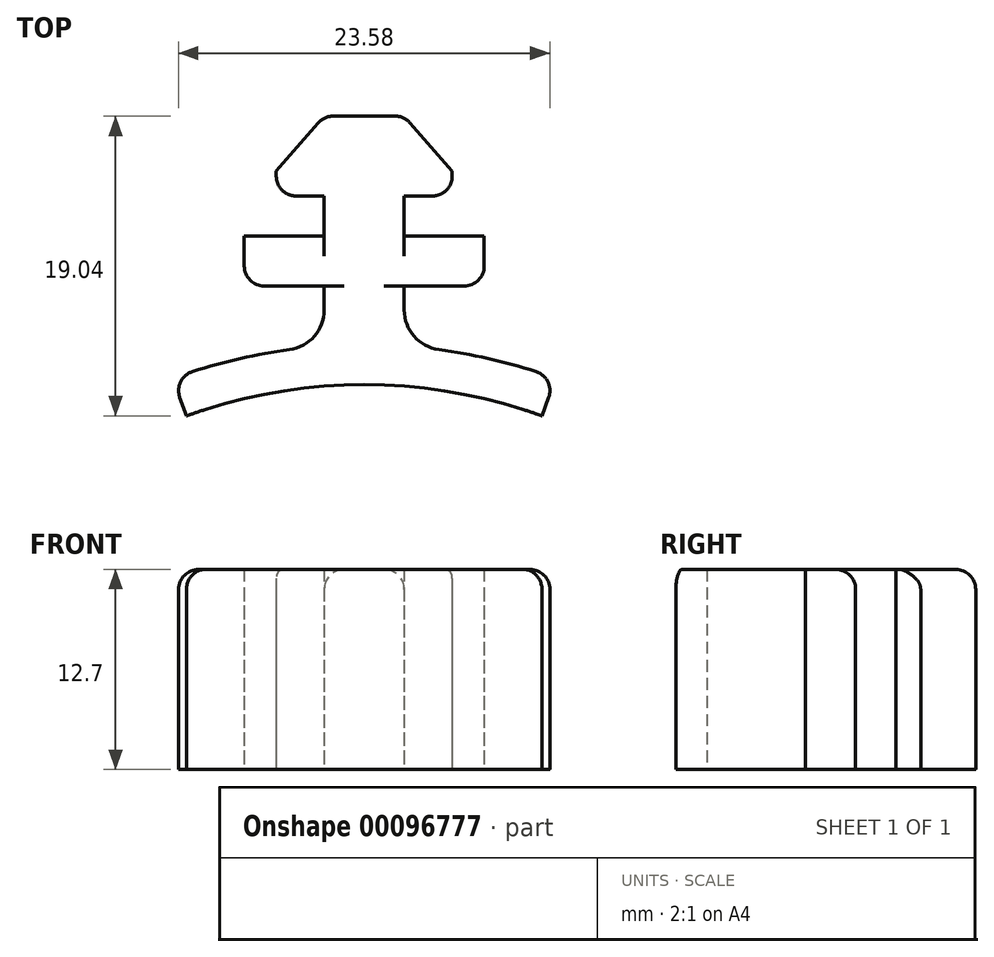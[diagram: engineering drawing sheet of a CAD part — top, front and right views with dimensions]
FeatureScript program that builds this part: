
annotation { "Feature Type Name" : "Feature", "Feature Type Description" : "" }
export const myFeature = defineFeature(function(context is Context, id is Id, definition is map)
    precondition{}
    {
        {
            var Q0;
            Q0=qCreatedBy(makeId("Top.planeOp"),FACE);
            var sketch = newSketch(context, id + "F0", { "sketchPlane" : qUnion([Q0])});
            skArc(sketch, "E0", {"start": v(11.29, 31) * mm, "mid": v(0, 33) * mm, "end": v(-11.29, 31) * mm});
            skArc(sketch, "E1.0", {"start": v(10.9, 33.82) * mm, "mid": v(7.86, 34.66) * mm, "end": v(4.74, 35.22) * mm});
            skLineSegment(sketch, "E2", {"start": v(0, 0) * mm, "end": v(0, 42.98) * mm, "construction": true});
            skLineSegment(sketch, "E3", {"start": v(11.29, 31) * mm, "end": v(11.71, 32.18) * mm});
            skLineSegment(sketch, "E4.MirrorCS", {"start": v(-11.29, 31) * mm, "end": v(-11.71, 32.18) * mm});
            skLineSegment(sketch, "E5", {"start": v(2.54, 37.74) * mm, "end": v(2.54, 39.26) * mm});
            skLineSegment(sketch, "E6.MirrorCS", {"start": v(-2.54, 37.74) * mm, "end": v(-2.54, 39.26) * mm});
            skLineSegment(sketch, "E7", {"start": v(2.54, 39.26) * mm, "end": v(6.35, 39.26) * mm});
            skLineSegment(sketch, "E8", {"start": v(7.62, 40.53) * mm, "end": v(7.62, 42.43) * mm});
            skLineSegment(sketch, "E9", {"start": v(7.62, 42.43) * mm, "end": v(2.54, 42.43) * mm});
            skLineSegment(sketch, "E10", {"start": v(2.54, 42.43) * mm, "end": v(2.54, 44.97) * mm});
            skLineSegment(sketch, "E11", {"start": v(2.54, 44.97) * mm, "end": v(4.32, 44.97) * mm});
            skLineSegment(sketch, "E12", {"start": v(5.59, 46.24) * mm, "end": v(5.59, 46.56) * mm});
            skLineSegment(sketch, "E13", {"start": v(5.59, 46.56) * mm, "end": v(2.92, 49.62) * mm});
            skLineSegment(sketch, "E14", {"start": v(1.96, 50.05) * mm, "end": v(0, 50.05) * mm});
            skLineSegment(sketch, "E15.MirrorCS", {"start": v(-5.59, 46.24) * mm, "end": v(-5.59, 46.56) * mm});
            skLineSegment(sketch, "E16.MirrorCS", {"start": v(-5.59, 46.56) * mm, "end": v(-2.92, 49.62) * mm});
            skLineSegment(sketch, "E17.MirrorCS", {"start": v(-2.54, 44.97) * mm, "end": v(-4.32, 44.97) * mm});
            skLineSegment(sketch, "E18.MirrorCS", {"start": v(-7.62, 42.43) * mm, "end": v(-2.54, 42.43) * mm});
            skLineSegment(sketch, "E19.MirrorCS", {"start": v(-2.54, 42.43) * mm, "end": v(-2.54, 44.97) * mm});
            skLineSegment(sketch, "E20.MirrorCS", {"start": v(-7.62, 40.53) * mm, "end": v(-7.62, 42.43) * mm});
            skLineSegment(sketch, "E21.MirrorCS", {"start": v(-2.54, 39.26) * mm, "end": v(-6.35, 39.26) * mm});
            skLineSegment(sketch, "E22.MirrorCS", {"start": v(-1.96, 50.05) * mm, "end": v(0, 50.05) * mm});
            skLineSegment(sketch, "E23.MirrorCS", {"start": v(-2.54, 50.05) * mm, "end": v(0, 50.05) * mm});
            skPoint(sketch, "E24.orphan", {"position": v(-15.23, 41.84) * mm});
            skPoint(sketch, "E25.orphan", {"position": v(15.23, 41.84) * mm});
            skArc(sketch, "E26.trimOffspring", {"start": v(-4.74, 35.22) * mm, "mid": v(-7.86, 34.66) * mm, "end": v(-10.9, 33.82) * mm});
            skPoint(sketch, "E27.visualSharp", {"position": v(-2.54, 35.45) * mm});
            skArc(sketch, "E27.filletArc", {"start": v(-4.74, 35.22) * mm, "mid": v(-3.17, 36.07) * mm, "end": v(-2.54, 37.74) * mm});
            skPoint(sketch, "E28.visualSharp", {"position": v(2.54, 35.45) * mm});
            skArc(sketch, "E28.filletArc", {"start": v(2.54, 37.74) * mm, "mid": v(3.17, 36.07) * mm, "end": v(4.74, 35.22) * mm});
            skPoint(sketch, "E29.visualSharp", {"position": v(-7.62, 39.26) * mm});
            skArc(sketch, "E29.filletArc", {"start": v(-7.62, 40.53) * mm, "mid": v(-7.25, 39.63) * mm, "end": v(-6.35, 39.26) * mm});
            skPoint(sketch, "E30.visualSharp", {"position": v(7.62, 39.26) * mm});
            skArc(sketch, "E30.filletArc", {"start": v(6.35, 39.26) * mm, "mid": v(7.25, 39.63) * mm, "end": v(7.62, 40.53) * mm});
            skPoint(sketch, "E31.visualSharp", {"position": v(12.16, 33.4) * mm});
            skArc(sketch, "E31.filletArc", {"start": v(11.71, 32.18) * mm, "mid": v(11.66, 33.17) * mm, "end": v(10.9, 33.82) * mm});
            skPoint(sketch, "E32.visualSharp", {"position": v(-12.16, 33.4) * mm});
            skArc(sketch, "E32.filletArc", {"start": v(-10.9, 33.82) * mm, "mid": v(-11.66, 33.17) * mm, "end": v(-11.71, 32.18) * mm});
            skPoint(sketch, "E33.visualSharp", {"position": v(-2.54, 50.05) * mm});
            skArc(sketch, "E33.filletArc", {"start": v(-1.96, 50.05) * mm, "mid": v(-2.49, 49.94) * mm, "end": v(-2.92, 49.62) * mm});
            skPoint(sketch, "E34.visualSharp", {"position": v(2.54, 50.05) * mm});
            skArc(sketch, "E34.filletArc", {"start": v(2.92, 49.62) * mm, "mid": v(2.49, 49.94) * mm, "end": v(1.96, 50.05) * mm});
            skPoint(sketch, "E35.visualSharp", {"position": v(-5.59, 44.97) * mm});
            skArc(sketch, "E35.filletArc", {"start": v(-5.59, 46.24) * mm, "mid": v(-5.22, 45.35) * mm, "end": v(-4.32, 44.97) * mm});
            skPoint(sketch, "E36.visualSharp", {"position": v(5.59, 44.97) * mm});
            skArc(sketch, "E36.filletArc", {"start": v(4.32, 44.97) * mm, "mid": v(5.22, 45.35) * mm, "end": v(5.59, 46.24) * mm});
            skSolve(sketch);
        }
        {
            var Q0;
            Q0=makeQuery(id+"F0.imprint","IMPRINT",FACE,{"disambiguationData":[TD([[makeQuery(id+"F0.imprint","IMPRINT",EDGE,{"derivedFrom":sQuery(id+"F0.wireOp",EDGE,"E0")}),-1.0]])]});
            extrude(context, id + "F1", {"entities" : qUnion([Q0]), "depth" : 12.7 * mm});
        }
        {
            var Q0;
            Q0=makeQuery(id+"F1.opExtrude","CAP_EDGE",EDGE,{"disambiguationData":[OSD([sQuery(id+"F0.wireOp",EDGE,"E28.filletArc")])],"isStart":false});
            var Q1;
            Q1=makeQuery(id+"F1.opExtrude","CAP_EDGE",EDGE,{"disambiguationData":[OSD([sQuery(id+"F0.wireOp",EDGE,"E26.trimOffspring")])],"isStart":false});
            var Q2;
            Q2=makeQuery(id+"F1.opExtrude","CAP_EDGE",EDGE,{"disambiguationData":[OSD([sQuery(id+"F0.wireOp",EDGE,"E18.MirrorCS")])],"isStart":false});
            var Q3;
            Q3=makeQuery(id+"F1.opExtrude","CAP_EDGE",EDGE,{"disambiguationData":[OSD([sQuery(id+"F0.wireOp",EDGE,"E9")])],"isStart":false});
            var Q4;
            Q4=makeQuery(id+"F1.opExtrude","CAP_EDGE",EDGE,{"disambiguationData":[OSD([sQuery(id+"F0.wireOp",EDGE,"E13")])],"isStart":false});
            fillet(context, id + "F2", {"entities" : qUnion([Q0, Q1, Q2, Q3, Q4]), "radius" : 1.27 * mm, "tangentPropagation" : true, "allowEdgeOverflow" : false});
        }
    });
